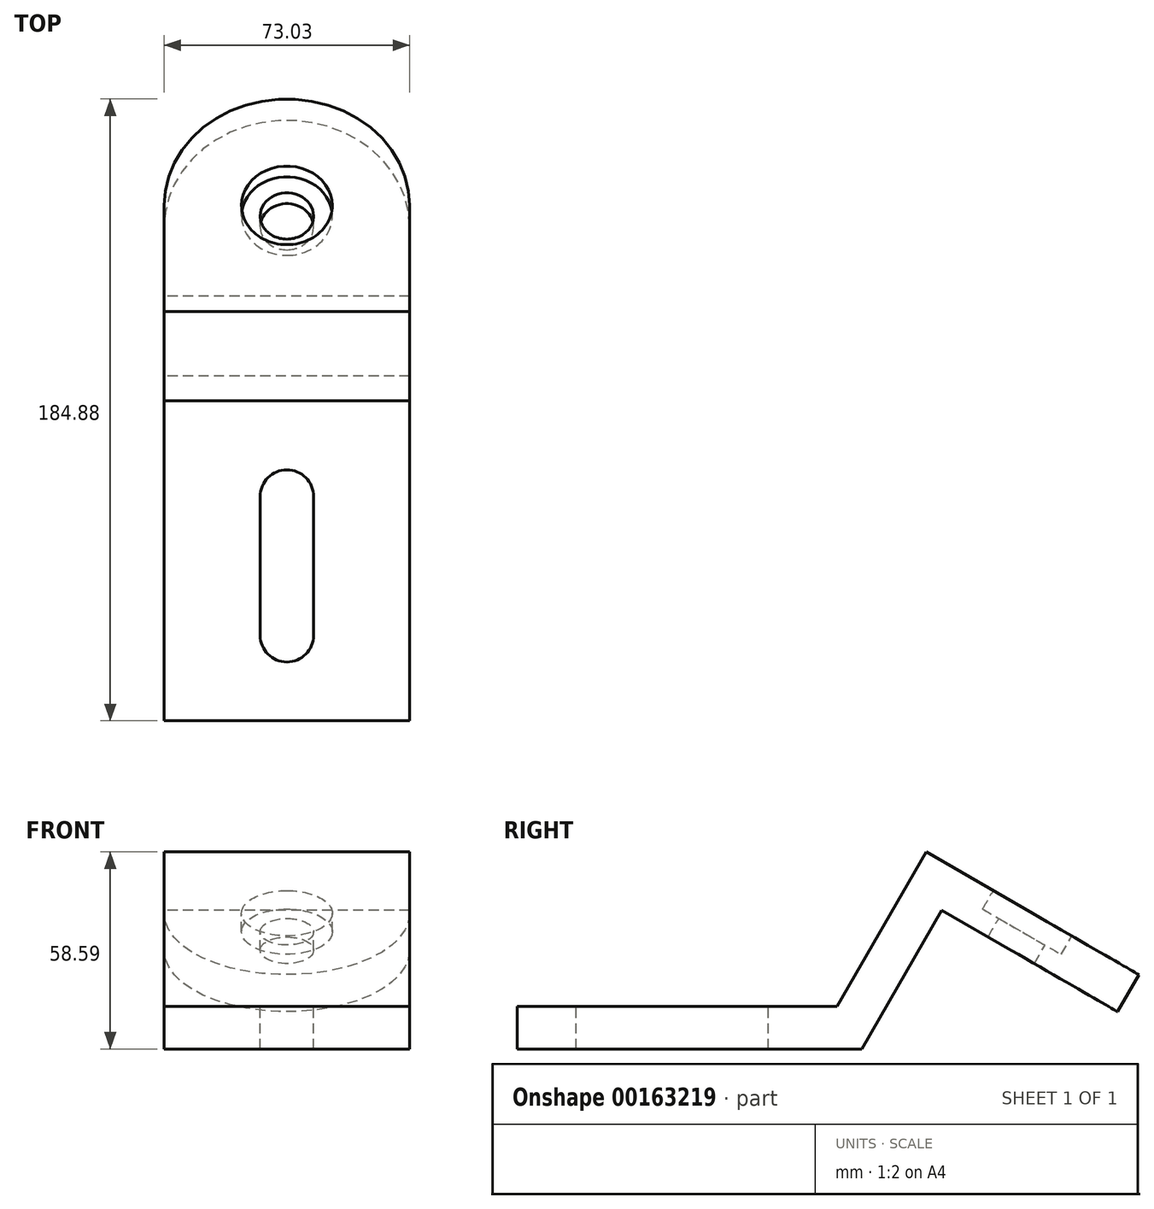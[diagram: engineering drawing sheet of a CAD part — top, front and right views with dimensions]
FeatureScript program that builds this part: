
annotation { "Feature Type Name" : "Feature", "Feature Type Description" : "" }
export const myFeature = defineFeature(function(context is Context, id is Id, definition is map)
    precondition{}
    {
        {
            var Q0;
            Q0=qCreatedBy(makeId("Right.planeOp"),FACE);
            var sketch = newSketch(context, id + "F0", { "sketchPlane" : qUnion([Q0])});
            skLineSegment(sketch, "E0.bottom", {"start": v(-47.57, 6.35) * mm, "end": v(47.57, 6.35) * mm});
            skLineSegment(sketch, "E0.top", {"start": v(-47.57, -6.35) * mm, "end": v(54.9, -6.35) * mm});
            skLineSegment(sketch, "E0.left", {"start": v(-47.57, 6.35) * mm, "end": v(-47.57, -6.35) * mm});
            skPoint(sketch, "E0.middle", {"position": v(0, 0) * mm});
            skLineSegment(sketch, "E1", {"start": v(47.57, 6.35) * mm, "end": v(74.06, 52.24) * mm});
            skLineSegment(sketch, "E2", {"start": v(74.06, 52.24) * mm, "end": v(105.68, 33.99) * mm});
            skLineSegment(sketch, "E3.0", {"start": v(78.71, 34.9) * mm, "end": v(99.33, 22.99) * mm});
            skLineSegment(sketch, "E3.1", {"start": v(54.9, -6.35) * mm, "end": v(78.71, 34.9) * mm});
            skPoint(sketch, "E0.right.end.orphan", {"position": v(47.57, -6.35) * mm});
            skLineSegment(sketch, "E4", {"start": v(99.33, 22.99) * mm, "end": v(105.68, 33.99) * mm});
            skSolve(sketch);
        }
        {
            var Q0;
            Q0=makeQuery(id+"F0.imprint","IMPRINT",FACE,{"disambiguationData":[TD([[makeQuery(id+"F0.imprint","IMPRINT",EDGE,{"derivedFrom":sQuery(id+"F0.wireOp",EDGE,"E0.bottom")}),-1.0]])]});
            extrude(context, id + "F1", {"entities" : qUnion([Q0]), "depth" : 73.02 * mm});
        }
        {
            var Q0;
            Q0=makeQuery(id+"F1.opExtrude","SWEPT_FACE",FACE,{"disambiguationData":[OSD([sQuery(id+"F0.wireOp",EDGE,"E2")])]});
            var sketch = newSketch(context, id + "F2", { "sketchPlane" : qUnion([Q0])});
            skArc(sketch, "E5", {"start": v(73.03, 74.53) * mm, "mid": v(36.51, 111.04) * mm, "end": v(0, 74.53) * mm});
            skLineSegment(sketch, "E6", {"start": v(73.03, 74.53) * mm, "end": v(0, 74.53) * mm});
            skSolve(sketch);
        }
        {
            var Q0;
            Q0=makeQuery(id+"F2.imprint","IMPRINT",FACE,{"disambiguationData":[TD([[makeQuery(id+"F2.imprint","IMPRINT",EDGE,{"derivedFrom":sQuery(id+"F2.wireOp",EDGE,"E5")}),1.0]])]});
            var Q1;
            Q1=makeQuery(id+"F1.opExtrude","SWEPT_FACE",FACE,{"disambiguationData":[OSD([sQuery(id+"F0.wireOp",EDGE,"E3.0")])]});
            extrude(context, id + "F3", {"entities" : qUnion([Q0]), "operationType" : NewBodyOperationType.ADD, "endBound" : BoundingType.UP_TO_SURFACE, "oppositeDirection" : true, "endBoundEntityFace" : qUnion([Q1]), "depth" : 25.4 * mm});
        }
        {
            var Q0;
            Q0=makeQuery(id+"F3.boolean.opBoolean","MERGE",FACE,{"derivedFrom":[makeQuery(id+"F1.opExtrude","SWEPT_FACE",FACE,{"disambiguationData":[OSD([sQuery(id+"F0.wireOp",EDGE,"E2")])]}),makeQuery(id+"F3.opExtrude","CAP_FACE",FACE,{"disambiguationData":[OSD([sQuery(id+"F2.wireOp",EDGE,"E5"),sQuery(id+"F2.wireOp",EDGE,"E6")])],"isStart":true})]});
            var sketch = newSketch(context, id + "F4", { "sketchPlane" : qUnion([Q0])});
            skPoint(sketch, "E7", {"position": v(36.51, 74.53) * mm});
            skSolve(sketch);
        }
        {
            var Q0;
            Q0=sQuery(id+"F4.wireOp",VERTEX,"E7");
            var Q1;
            Q1=makeQuery(id+"F1.opExtrude","SWEPT_BODY",BODY,{"disambiguationData":[OSD([sQuery(id+"F0.wireOp",EDGE,"E0.bottom"),sQuery(id+"F0.wireOp",EDGE,"E0.top"),sQuery(id+"F0.wireOp",EDGE,"E0.left"),sQuery(id+"F0.wireOp",EDGE,"E1"),sQuery(id+"F0.wireOp",EDGE,"E2"),sQuery(id+"F0.wireOp",EDGE,"E3.0"),sQuery(id+"F0.wireOp",EDGE,"E3.1"),sQuery(id+"F0.wireOp",EDGE,"E4")])]});
            hole(context, id + "F5", {"style" : HoleStyle.C_BORE, "endStyle" : HoleEndStyle.THROUGH, "holeDiameter" : 15.88 * mm, "cBoreDiameter" : 26.99 * mm, "cBoreDepth" : 6.35 * mm, "locations" : qUnion([Q0]), "scope" : qUnion([Q1]), "isTappedThrough" : true});
        }
        {
            var Q0;
            Q0=makeQuery(id+"F1.opExtrude","SWEPT_FACE",FACE,{"disambiguationData":[OSD([sQuery(id+"F0.wireOp",EDGE,"E0.bottom")])]});
            var sketch = newSketch(context, id + "F6", { "sketchPlane" : qUnion([Q0])});
            skArc(sketch, "E8", {"start": v(28.58, -22.17) * mm, "mid": v(36.51, -30.1) * mm, "end": v(44.45, -22.17) * mm});
            skPoint(sketch, "E8.centerSnap0", {"position": v(36.51, -47.57) * mm});
            skArc(sketch, "E9", {"start": v(44.45, 19.1) * mm, "mid": v(36.51, 27.05) * mm, "end": v(28.57, 19.1) * mm});
            skLineSegment(sketch, "E10", {"start": v(44.45, -22.17) * mm, "end": v(44.45, 19.1) * mm});
            skLineSegment(sketch, "E11", {"start": v(28.58, -22.17) * mm, "end": v(28.57, 19.1) * mm});
            skSolve(sketch);
        }
        {
            var Q0;
            Q0=makeQuery(id+"F6.imprint","IMPRINT",FACE,{"disambiguationData":[TD([[makeQuery(id+"F6.imprint","IMPRINT",EDGE,{"derivedFrom":sQuery(id+"F6.wireOp",EDGE,"E8")}),1.0]])]});
            extrude(context, id + "F7", {"entities" : qUnion([Q0]), "operationType" : NewBodyOperationType.REMOVE, "endBound" : BoundingType.THROUGH_ALL, "oppositeDirection" : true, "depth" : 25.4 * mm});
        }
    });
